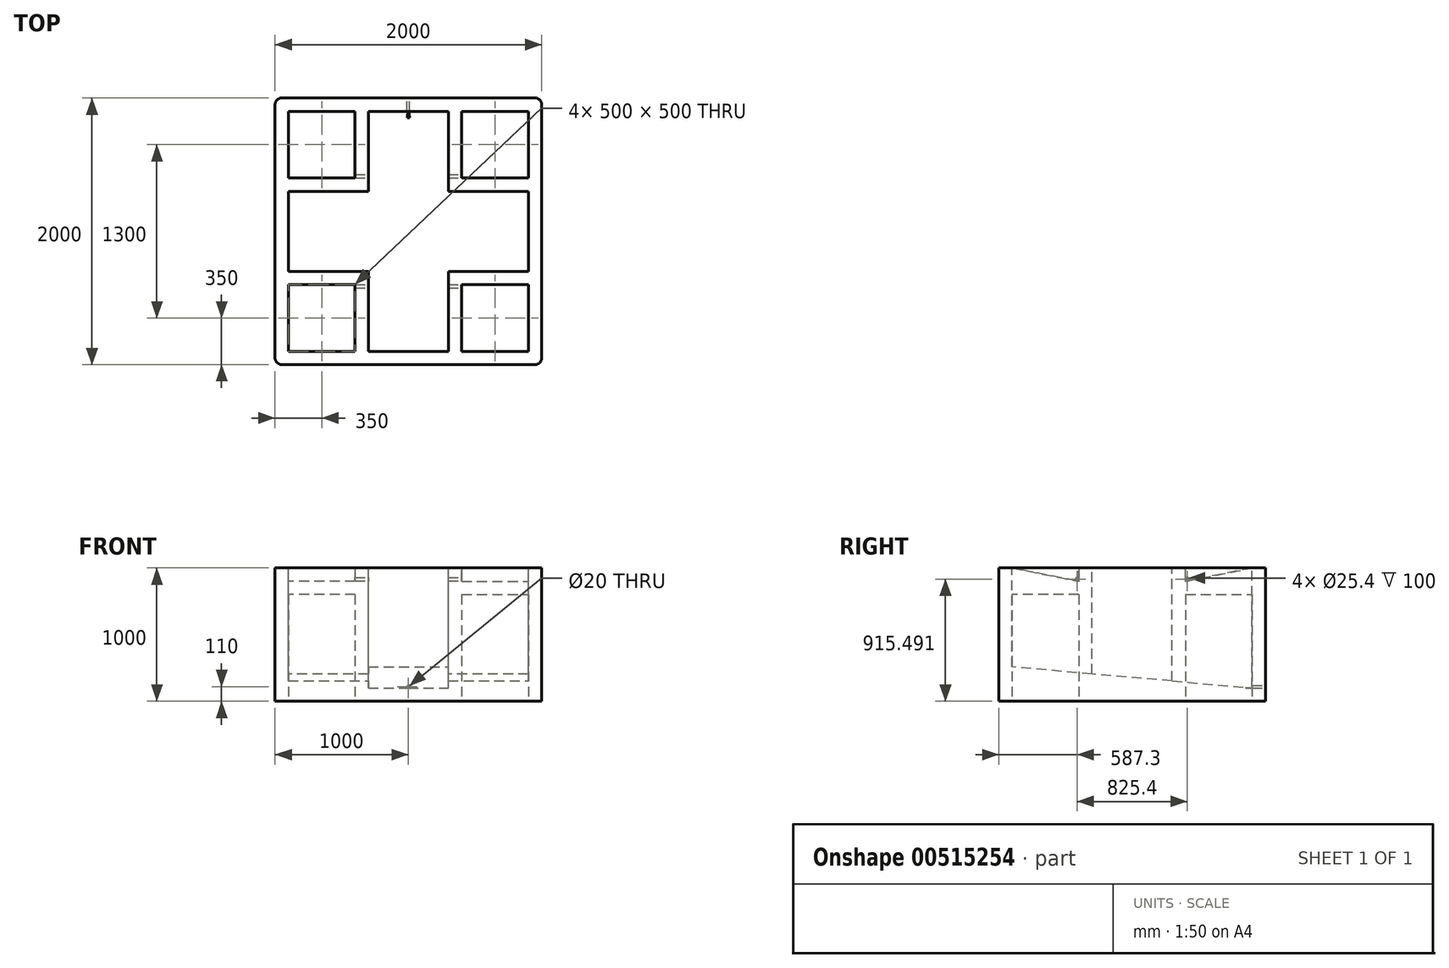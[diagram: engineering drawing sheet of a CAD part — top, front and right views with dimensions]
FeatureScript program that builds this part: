
annotation { "Feature Type Name" : "Feature", "Feature Type Description" : "" }
export const myFeature = defineFeature(function(context is Context, id is Id, definition is map)
    precondition{}
    {
        {
            var Q0;
            Q0=qCreatedBy(makeId("Top.planeOp"),FACE);
            var sketch = newSketch(context, id + "F0", { "sketchPlane" : qUnion([Q0])});
            skLineSegment(sketch, "E0.bottom", {"start": v(1000, -1000) * mm, "end": v(-1000, -1000) * mm});
            skLineSegment(sketch, "E0.top", {"start": v(1000, 1000) * mm, "end": v(-1000, 1000) * mm});
            skLineSegment(sketch, "E0.left", {"start": v(1000, -1000) * mm, "end": v(1000, 1000) * mm});
            skLineSegment(sketch, "E0.right", {"start": v(-1000, -1000) * mm, "end": v(-1000, 1000) * mm});
            skPoint(sketch, "E0.middle", {"position": v(0, 0) * mm});
            skSolve(sketch);
        }
        {
            var Q0;
            Q0=makeQuery(id+"F0.imprint","IMPRINT",FACE,{"disambiguationData":[TD([[makeQuery(id+"F0.imprint","IMPRINT",EDGE,{"derivedFrom":sQuery(id+"F0.wireOp",EDGE,"E0.bottom")}),-1.0]])]});
            extrude(context, id + "F1", {"entities" : qUnion([Q0]), "depth" : 1000 * mm, "offsetDistance" : 25 * mm});
        }
        {
            var Q0;
            Q0=makeQuery(id+"F1.opExtrude","SWEPT_FACE",FACE,{"disambiguationData":[OSD([sQuery(id+"F0.wireOp",EDGE,"E0.right")])]});
            cPlane(context, id + "F2", {"entities" : qUnion([Q0]), "cplaneType" : CPlaneType.OFFSET, "offset" : 100 * mm, "oppositeDirection" : true, "width" : 150 * mm, "height" : 150 * mm});
        }
        {
            var Q0;
            Q0=makeQuery(id+"F1.opExtrude","SWEPT_FACE",FACE,{"disambiguationData":[OSD([sQuery(id+"F0.wireOp",EDGE,"E0.left")])]});
            cPlane(context, id + "F3", {"entities" : qUnion([Q0]), "cplaneType" : CPlaneType.OFFSET, "offset" : 100 * mm, "oppositeDirection" : true, "width" : 150 * mm, "height" : 150 * mm});
        }
        {
            var Q0;
            Q0=qCreatedBy(makeId("Right.planeOp"),FACE);
            cPlane(context, id + "F4", {"entities" : qUnion([Q0]), "cplaneType" : CPlaneType.OFFSET, "offset" : 250 * mm, "oppositeDirection" : true, "width" : 150 * mm, "height" : 150 * mm});
        }
        {
            var Q0;
            Q0=makeQuery(id+"F1.opExtrude","CAP_FACE",FACE,{"disambiguationData":[OSD([sQuery(id+"F0.wireOp",EDGE,"E0.bottom"),sQuery(id+"F0.wireOp",EDGE,"E0.top"),sQuery(id+"F0.wireOp",EDGE,"E0.left"),sQuery(id+"F0.wireOp",EDGE,"E0.right")])],"isStart":true});
            var sketch = newSketch(context, id + "F5", { "sketchPlane" : qUnion([Q0])});
            skLineSegment(sketch, "E1.0", {"start": v(-100, 400) * mm, "end": v(-700, 400) * mm});
            skLineSegment(sketch, "E2.0", {"start": v(-100, 400) * mm, "end": v(-100, -400) * mm});
            skLineSegment(sketch, "E3.0", {"start": v(-100, -400) * mm, "end": v(-700, -400) * mm});
            skLineSegment(sketch, "E4.0", {"start": v(-700, 400) * mm, "end": v(-700, -400) * mm});
            skSolve(sketch);
        }
        {
            var Q0;
            Q0=makeQuery(id+"F1.opExtrude","CAP_FACE",FACE,{"disambiguationData":[OSD([sQuery(id+"F0.wireOp",EDGE,"E0.bottom"),sQuery(id+"F0.wireOp",EDGE,"E0.top"),sQuery(id+"F0.wireOp",EDGE,"E0.left"),sQuery(id+"F0.wireOp",EDGE,"E0.right")])],"isStart":false});
            var sketch = newSketch(context, id + "F6", { "sketchPlane" : qUnion([Q0])});
            skLineSegment(sketch, "E5", {"start": v(-900, 300) * mm, "end": v(-900, -300) * mm});
            skLineSegment(sketch, "E6", {"start": v(-900, -300) * mm, "end": v(-300, -300) * mm});
            skLineSegment(sketch, "E7", {"start": v(-300, -300) * mm, "end": v(-300, -900) * mm});
            skLineSegment(sketch, "E8", {"start": v(-300, -900) * mm, "end": v(300, -900) * mm});
            skLineSegment(sketch, "E9", {"start": v(300, -900) * mm, "end": v(300, -300) * mm});
            skLineSegment(sketch, "E10", {"start": v(300, -300) * mm, "end": v(900, -300) * mm});
            skLineSegment(sketch, "E11", {"start": v(900, -300) * mm, "end": v(900, 300) * mm});
            skLineSegment(sketch, "E12", {"start": v(900, 300) * mm, "end": v(300, 300) * mm});
            skLineSegment(sketch, "E13", {"start": v(300, 300) * mm, "end": v(300, 900) * mm});
            skLineSegment(sketch, "E14", {"start": v(300, 900) * mm, "end": v(-300, 900) * mm});
            skLineSegment(sketch, "E15", {"start": v(-300, 900) * mm, "end": v(-300, 300) * mm});
            skLineSegment(sketch, "E16", {"start": v(-300, 300) * mm, "end": v(-900, 300) * mm});
            skSolve(sketch);
        }
        {
            var Q0;
            Q0=makeQuery(id+"F6.imprint","IMPRINT",FACE,{"disambiguationData":[TD([[makeQuery(id+"F6.imprint","IMPRINT",EDGE,{"derivedFrom":sQuery(id+"F6.wireOp",EDGE,"E5")}),1.0]])]});
            var Q1;
            Q1=makeQuery(id+"F1.opExtrude","CAP_FACE",FACE,{"disambiguationData":[OSD([sQuery(id+"F0.wireOp",EDGE,"E0.bottom"),sQuery(id+"F0.wireOp",EDGE,"E0.top"),sQuery(id+"F0.wireOp",EDGE,"E0.left"),sQuery(id+"F0.wireOp",EDGE,"E0.right")])],"isStart":true});
            extrude(context, id + "F7", {"entities" : qUnion([Q0]), "operationType" : NewBodyOperationType.REMOVE, "endBound" : BoundingType.UP_TO_SURFACE, "oppositeDirection" : true, "depth" : 25 * mm, "endBoundEntityFace" : qUnion([Q1]), "hasOffset" : true, "offsetDistance" : 100 * mm});
        }
        {
            var Q0;
            Q0=qCreatedBy(id+"F2.planeOp",FACE);
            var sketch = newSketch(context, id + "F8", { "sketchPlane" : qUnion([Q0])});
            skLineSegment(sketch, "E17.0", {"start": v(900, 1000) * mm, "end": v(400, 1000) * mm});
            skLineSegment(sketch, "E18", {"start": v(900, 1000) * mm, "end": v(400, 900) * mm});
            skLineSegment(sketch, "E19", {"start": v(400, 900) * mm, "end": v(400, 1000) * mm});
            skPoint(sketch, "E20.orphan", {"position": v(-1000, 1000) * mm});
            skPoint(sketch, "E21.orphan", {"position": v(1000, 1000) * mm});
            skLineSegment(sketch, "E22", {"start": v(400, 900) * mm, "end": v(-400, 900) * mm, "construction": true});
            skLineSegment(sketch, "E23", {"start": v(-400, 900) * mm, "end": v(-900, 1000) * mm});
            skLineSegment(sketch, "E24", {"start": v(-400, 900) * mm, "end": v(-400, 1000) * mm});
            skLineSegment(sketch, "E25", {"start": v(-400, 1000) * mm, "end": v(-900, 1000) * mm});
            skSolve(sketch);
        }
        {
            var Q0;
            Q0 = qSketchRegion(id + "F8", true);
            var Q1;
            Q1=makeQuery(id+"F7.boolean.opBoolean","COPY",FACE,{"derivedFrom":makeQuery(id+"F7.opExtrude","SWEPT_FACE",FACE,{"disambiguationData":[OSD([sQuery(id+"F6.wireOp",EDGE,"E7")])]})});
            extrude(context, id + "F9", {"entities" : qUnion([Q0]), "operationType" : NewBodyOperationType.REMOVE, "endBound" : BoundingType.UP_TO_SURFACE, "oppositeDirection" : true, "depth" : 25 * mm, "endBoundEntityFace" : qUnion([Q1]), "hasOffset" : true, "offsetDistance" : 100 * mm});
        }
        {
            var Q0;
            Q0=qCreatedBy(id+"F3.planeOp",FACE);
            var sketch = newSketch(context, id + "F10", { "sketchPlane" : qUnion([Q0])});
            skLineSegment(sketch, "E26.0.0", {"start": v(400, 1000) * mm, "end": v(400, 900) * mm});
            skLineSegment(sketch, "E26.0.1", {"start": v(400, 900) * mm, "end": v(900, 1000) * mm});
            skLineSegment(sketch, "E26.0.2", {"start": v(900, 1000) * mm, "end": v(400, 1000) * mm});
            skLineSegment(sketch, "E27.0.0", {"start": v(-400, 900) * mm, "end": v(-400, 1000) * mm});
            skLineSegment(sketch, "E27.0.1", {"start": v(-400, 1000) * mm, "end": v(-900, 1000) * mm});
            skLineSegment(sketch, "E27.0.2", {"start": v(-900, 1000) * mm, "end": v(-400, 900) * mm});
            skSolve(sketch);
        }
        {
            var Q0;
            Q0 = qSketchRegion(id + "F10", true);
            var Q1;
            Q1=makeQuery(id+"F7.boolean.opBoolean","COPY",FACE,{"derivedFrom":makeQuery(id+"F7.opExtrude","SWEPT_FACE",FACE,{"disambiguationData":[OSD([sQuery(id+"F6.wireOp",EDGE,"E13")])]})});
            extrude(context, id + "F11", {"entities" : qUnion([Q0]), "operationType" : NewBodyOperationType.REMOVE, "endBound" : BoundingType.UP_TO_SURFACE, "oppositeDirection" : true, "depth" : 25 * mm, "endBoundEntityFace" : qUnion([Q1]), "hasOffset" : true, "offsetDistance" : 100 * mm});
        }
        {
            var Q0;
            Q0=qCreatedBy(id+"F3.planeOp",FACE);
            var sketch = newSketch(context, id + "F12", { "sketchPlane" : qUnion([Q0])});
            skLineSegment(sketch, "E28.0", {"start": v(-300, 100) * mm, "end": v(-900, 100) * mm});
            skLineSegment(sketch, "E29.0", {"start": v(300, 100) * mm, "end": v(-300, 100) * mm});
            skLineSegment(sketch, "E30.0", {"start": v(900, 100) * mm, "end": v(300, 100) * mm});
            skLineSegment(sketch, "E31", {"start": v(900, 100) * mm, "end": v(-900, 257.48) * mm});
            skLineSegment(sketch, "E32", {"start": v(-900, 257.48) * mm, "end": v(-900, 100) * mm});
            skSolve(sketch);
        }
        {
            var Q0;
            Q0 = qSketchRegion(id + "F12", true);
            var Q1;
            Q1=makeQuery(id+"F7.boolean.opBoolean","COPY",FACE,{"derivedFrom":makeQuery(id+"F7.opExtrude","SWEPT_FACE",FACE,{"disambiguationData":[OSD([sQuery(id+"F6.wireOp",EDGE,"E5")])]})});
            extrude(context, id + "F13", {"entities" : qUnion([Q0]), "operationType" : NewBodyOperationType.ADD, "endBound" : BoundingType.UP_TO_SURFACE, "oppositeDirection" : true, "depth" : 25 * mm, "endBoundEntityFace" : qUnion([Q1]), "offsetDistance" : 25 * mm});
        }
        {
            var Q0;
            Q0=makeQuery(id+"F5.imprint","IMPRINT",FACE,{"disambiguationData":[TD([[makeQuery(id+"F5.imprint","IMPRINT",EDGE,{"derivedFrom":sQuery(id+"F5.wireOp",EDGE,"E1.0")}),-1.0]])]});
            var sketch = newSketch(context, id + "F14", { "sketchPlane" : qUnion([Q0])});
            skLineSegment(sketch, "E33.0", {"start": v(-900, -400) * mm, "end": v(-900, -900) * mm});
            skLineSegment(sketch, "E34.0", {"start": v(-400, -400) * mm, "end": v(-900, -400) * mm});
            skLineSegment(sketch, "E35.0", {"start": v(-400, -900) * mm, "end": v(-400, -400) * mm});
            skLineSegment(sketch, "E36.0", {"start": v(-400, -900) * mm, "end": v(-900, -900) * mm});
            skLineSegment(sketch, "E37.0", {"start": v(400, -900) * mm, "end": v(900, -900) * mm});
            skLineSegment(sketch, "E38.0", {"start": v(400, -400) * mm, "end": v(400, -900) * mm});
            skLineSegment(sketch, "E39.0", {"start": v(400, -400) * mm, "end": v(900, -400) * mm});
            skLineSegment(sketch, "E40.0", {"start": v(900, -900) * mm, "end": v(900, -400) * mm});
            skLineSegment(sketch, "E41.0", {"start": v(400, 400) * mm, "end": v(900, 400) * mm});
            skLineSegment(sketch, "E42.0", {"start": v(400, 900) * mm, "end": v(400, 400) * mm});
            skLineSegment(sketch, "E43.0", {"start": v(400, 900) * mm, "end": v(900, 900) * mm});
            skLineSegment(sketch, "E44.0", {"start": v(900, 400) * mm, "end": v(900, 900) * mm});
            skLineSegment(sketch, "E45.0", {"start": v(-400, 400) * mm, "end": v(-400, 900) * mm});
            skLineSegment(sketch, "E46.0", {"start": v(-400, 400) * mm, "end": v(-900, 400) * mm});
            skLineSegment(sketch, "E47.0", {"start": v(-900, 900) * mm, "end": v(-900, 400) * mm});
            skLineSegment(sketch, "E48.0", {"start": v(-400, 900) * mm, "end": v(-900, 900) * mm});
            skSolve(sketch);
        }
        {
            var Q0;
            Q0 = qSketchRegion(id + "F14", true);
            var Q1;
            Q1=makeQuery(id+"F1.opExtrude","CAP_FACE",FACE,{"disambiguationData":[OSD([sQuery(id+"F0.wireOp",EDGE,"E0.bottom"),sQuery(id+"F0.wireOp",EDGE,"E0.top"),sQuery(id+"F0.wireOp",EDGE,"E0.left"),sQuery(id+"F0.wireOp",EDGE,"E0.right")])],"isStart":false});
            extrude(context, id + "F15", {"entities" : qUnion([Q0]), "operationType" : NewBodyOperationType.REMOVE, "endBound" : BoundingType.UP_TO_SURFACE, "oppositeDirection" : true, "depth" : 25 * mm, "endBoundEntityFace" : qUnion([Q1]), "hasOffset" : true, "offsetDistance" : 200 * mm});
        }
        {
            var Q0;
            Q0=qCreatedBy(id+"F3.planeOp",FACE);
            var sketch = newSketch(context, id + "F16", { "sketchPlane" : qUnion([Q0])});
            skCircle(sketch, "E49", {"center": v(-412.7, 915.5) * mm, "radius": 12.7 * mm});
            skCircle(sketch, "E50", {"center": v(412.7, 915.5) * mm, "radius": 12.7 * mm});
            skSolve(sketch);
        }
        {
            var Q0;
            Q0 = qSketchRegion(id + "F16", true);
            var Q1;
            Q1=qCreatedBy(id+"F2.planeOp",FACE);
            extrude(context, id + "F17", {"entities" : qUnion([Q0]), "operationType" : NewBodyOperationType.REMOVE, "endBound" : BoundingType.UP_TO_SURFACE, "oppositeDirection" : true, "depth" : 25 * mm, "endBoundEntityFace" : qUnion([Q1]), "offsetDistance" : 25 * mm});
        }
        {
            var Q0;
            Q0=makeQuery(id+"F1.opExtrude","SWEPT_FACE",FACE,{"disambiguationData":[OSD([sQuery(id+"F0.wireOp",EDGE,"E0.top")])]});
            var sketch = newSketch(context, id + "F18", { "sketchPlane" : qUnion([Q0])});
            skCircle(sketch, "E51", {"center": v(0, 110) * mm, "radius": 10 * mm});
            skSolve(sketch);
        }
        {
            var Q0;
            Q0 = qSketchRegion(id + "F18", true);
            extrude(context, id + "F19", {"entities" : qUnion([Q0]), "operationType" : NewBodyOperationType.REMOVE, "oppositeDirection" : true, "depth" : 150 * mm, "offsetDistance" : 25 * mm});
        }
        {
            var Q0;
            Q0=makeQuery(id+"F1.opExtrude","SWEPT_EDGE",EDGE,{"disambiguationData":[OSD([sQuery(id+"F0.wireOp",EDGE,"E0.bottom"),sQuery(id+"F0.wireOp",EDGE,"E0.left")])]});
            var Q1;
            Q1=makeQuery(id+"F1.opExtrude","SWEPT_EDGE",EDGE,{"disambiguationData":[OSD([sQuery(id+"F0.wireOp",EDGE,"E0.top"),sQuery(id+"F0.wireOp",EDGE,"E0.left")])]});
            var Q2;
            Q2=makeQuery(id+"F1.opExtrude","SWEPT_EDGE",EDGE,{"disambiguationData":[OSD([sQuery(id+"F0.wireOp",EDGE,"E0.top"),sQuery(id+"F0.wireOp",EDGE,"E0.right")])]});
            var Q3;
            Q3=makeQuery(id+"F1.opExtrude","SWEPT_EDGE",EDGE,{"disambiguationData":[OSD([sQuery(id+"F0.wireOp",EDGE,"E0.bottom"),sQuery(id+"F0.wireOp",EDGE,"E0.right")])]});
            fillet(context, id + "F20", {"entities" : qUnion([Q0, Q1, Q2, Q3]), "radius" : 50 * mm, "tangentPropagation" : true, "allowEdgeOverflow" : false});
        }
    });
